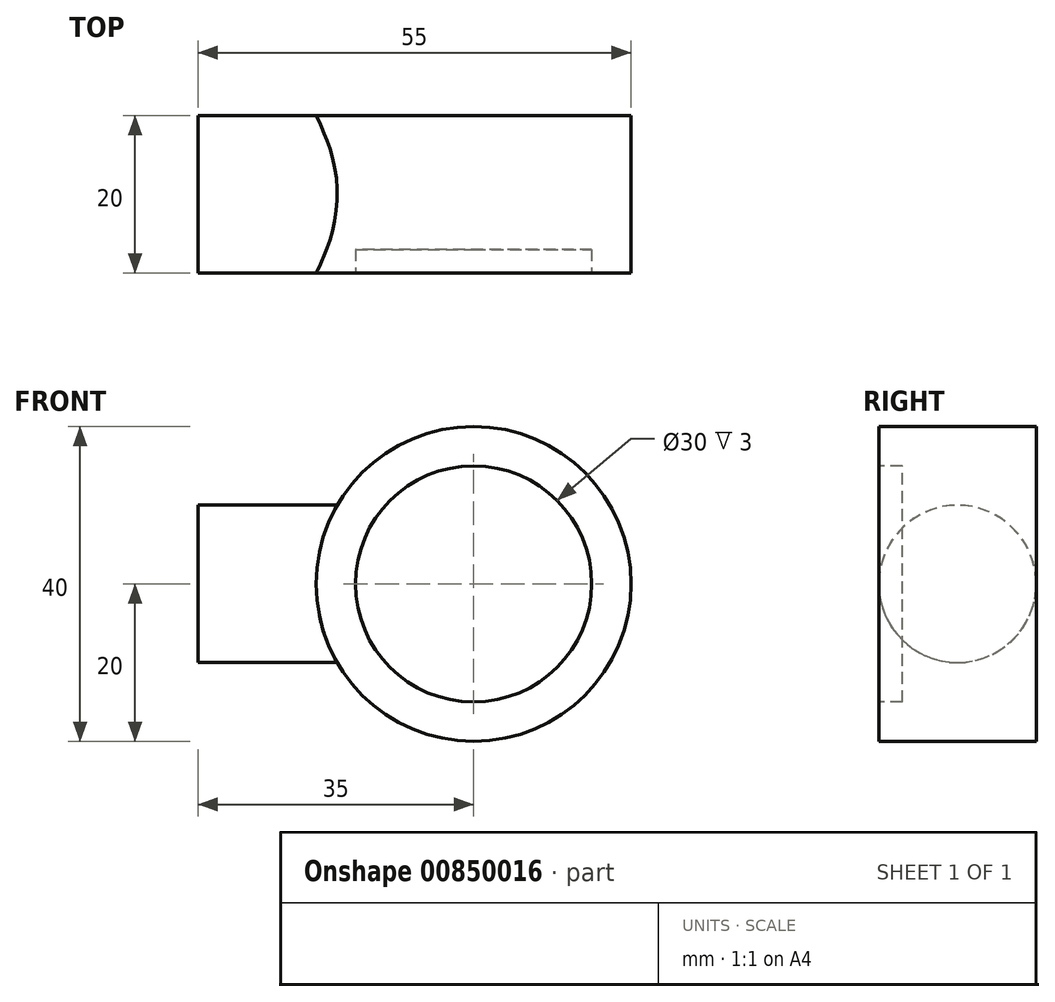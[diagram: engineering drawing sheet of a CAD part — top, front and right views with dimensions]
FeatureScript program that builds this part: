
annotation { "Feature Type Name" : "Feature", "Feature Type Description" : "" }
export const myFeature = defineFeature(function(context is Context, id is Id, definition is map)
    precondition{}
    {
        {
            var Q0;
            Q0=qCreatedBy(makeId("Front.planeOp"),FACE);
            var sketch = newSketch(context, id + "F0", { "sketchPlane" : qUnion([Q0])});
            skCircle(sketch, "E0", {"center": v(0, 0) * mm, "radius": 20 * mm});
            skSolve(sketch);
        }
        {
            var Q0;
            Q0=makeQuery(id+"F0.imprint","IMPRINT",FACE,{"disambiguationData":[TD([[makeQuery(id+"F0.imprint","IMPRINT",EDGE,{"derivedFrom":sQuery(id+"F0.wireOp",EDGE,"E0")}),1.0]])]});
            extrude(context, id + "F1", {"entities" : qUnion([Q0]), "endBound" : BoundingType.SYMMETRIC, "depth" : 20 * mm, "offsetDistance" : 25 * mm});
        }
        {
            var Q0;
            Q0=qCreatedBy(makeId("Right.planeOp"),FACE);
            cPlane(context, id + "F2", {"entities" : qUnion([Q0]), "cplaneType" : CPlaneType.OFFSET, "offset" : 35 * mm, "oppositeDirection" : true, "width" : 150 * mm, "height" : 150 * mm});
        }
        {
            var Q0;
            Q0=qCreatedBy(id+"F2.planeOp",FACE);
            var sketch = newSketch(context, id + "F3", { "sketchPlane" : qUnion([Q0])});
            skCircle(sketch, "E1", {"center": v(0, 0) * mm, "radius": 10 * mm});
            skSolve(sketch);
        }
        {
            var Q0;
            Q0=makeQuery(id+"F3.imprint","IMPRINT",FACE,{"disambiguationData":[TD([[makeQuery(id+"F3.imprint","IMPRINT",EDGE,{"derivedFrom":sQuery(id+"F3.wireOp",EDGE,"E1")}),1.0]])]});
            var Q1;
            Q1=makeQuery(id+"F1.opExtrude","SWEPT_FACE",FACE,{"disambiguationData":[OSD([sQuery(id+"F0.wireOp",EDGE,"E0")])]});
            extrude(context, id + "F4", {"entities" : qUnion([Q0]), "operationType" : NewBodyOperationType.ADD, "endBound" : BoundingType.UP_TO_SURFACE, "depth" : 3 * mm, "endBoundEntityFace" : qUnion([Q1]), "offsetDistance" : 25 * mm});
        }
        {
            var Q0;
            Q0=makeQuery(id+"F1.opExtrude","CAP_FACE",FACE,{"disambiguationData":[OSD([sQuery(id+"F0.wireOp",EDGE,"E0")])],"isStart":false});
            var sketch = newSketch(context, id + "F5", { "sketchPlane" : qUnion([Q0])});
            skCircle(sketch, "E2", {"center": v(0, 0) * mm, "radius": 15 * mm});
            skSolve(sketch);
        }
        {
            var Q0;
            Q0=makeQuery(id+"F5.imprint","IMPRINT",FACE,{"disambiguationData":[TD([[makeQuery(id+"F5.imprint","IMPRINT",EDGE,{"derivedFrom":sQuery(id+"F5.wireOp",EDGE,"E2")}),1.0]])]});
            extrude(context, id + "F6", {"entities" : qUnion([Q0]), "operationType" : NewBodyOperationType.REMOVE, "oppositeDirection" : true, "depth" : 3 * mm, "offsetDistance" : 25 * mm});
        }
    });
